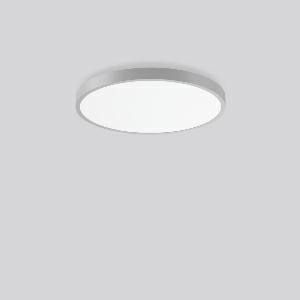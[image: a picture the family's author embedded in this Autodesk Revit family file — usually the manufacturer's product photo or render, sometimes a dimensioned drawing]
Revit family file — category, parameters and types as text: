
# Revit family: triona_round_a_312384_004_76_f7ac
name_source: partatom
category: Lighting Fixtures
units: mm (PartAtom-declared; Revit-internal decimal feet)

## family parameters
Cut with Voids When Loaded = No
Host = Face
Light Source = No
Part Type = Normal
Room Calculation Point = No
Round Connector Dimension = Use Diameter
Shared = No

## types (1)
- TRIONA round A (1 x LED Modul 830, 9300 lm, 3000)
    Apparent Load = 106 VA
    CIE Flux Codes = 49 80 96 72 100
    Color Rendering = 80
    Color Temperature = 3000
    Default Elevation = 1800 mm
    Description = Series: TRIONA round
Decorative round LED surface-mounted luminaire. Flat, seamless frame: aluminium extrusion profile, powder coated. Cover made of sheet steel, powder-coated. Direct light emission through a diffuser plastic opal. Indirect light emission through a flush diffuser made of satin-finish plastic. Lightguide and diffuser made of non-yellowing plastic (PMMA). Lateral light emission (RZB SIDELITE technology) for above-average homogeneous light distribution. Direct 70%, indirect 30% light emission. Suitable for Ceiling mounting, Wall (surface). Tool-free mounting via bayonet connection. Electronic ballast included. Very easy installation thanks to Plug+Play connection. 
Colour: silver, matt (approx. RAL 9006)
Diameter: 681 mm
Height: 88 mm
Lamp: LED
Socket: without socket
Colour temperature: 3000K
Colour rendering index (CRI): 80
System power: 106 W
Rated luminous flux: 9300 lm
Luminous efficiency: 88 lm/W
Control gear: Converter, dimmable, DALI
Protection class: I
Type of protection: IP 20
    Height = 88 mm
    Lamp = 1 x LED Modul 830
    Lamp Light Flux = 9300 lm
    Lamp count = 1
    Length = 681 mm
    Lifetime = 50000 h
    Luminous efficacy = 88 lm/W
    Manufacturer = RZB
    ModVariant = No
    Model = 312384.004.76
    Mounting Place = Ceiling
    Mounting Type = Surface mounted
    Number of Poles = 1
    OnlyDefault = Yes
    Power Factor = 1
    Product Name = TRIONA round A
    Product group = Surface mounted modular luminaires
    ProductGroupID = 306
    Protection Class = Protection class I
    Protection Degree = IP 20
    RLX_Detail_Level = 1
    RLX_Emergency_Light_Flux = 0 lm
    RLX_Emergency_Type = 0
    RLX_Emergency_Type_DB = No
    RlxData = <blob elided: 40261 chars, md5=290e9a28>
    Socket = socket
    Standby Power = 0 W
    System Light Flux = 9300 lm
    System Power = 106 W
    Type Comments = Product without accessories
    Type Image = 312384.004.jpg
    URL = http://relux.com
    VarID = ---
    Voltage = 230 V
    Voltage Range = 220-240 V
    Weight = 0.00 kg
    Width = 0 mm  [stored 0 ft]

note: [stored X ft] marks values corroborated as IEEE doubles in the binary element streams (Revit-internal decimal feet)

## geometry (parser evidence)
native form markers: Blend x4, Sweep x13
no freeform markers — native parametric forms only
